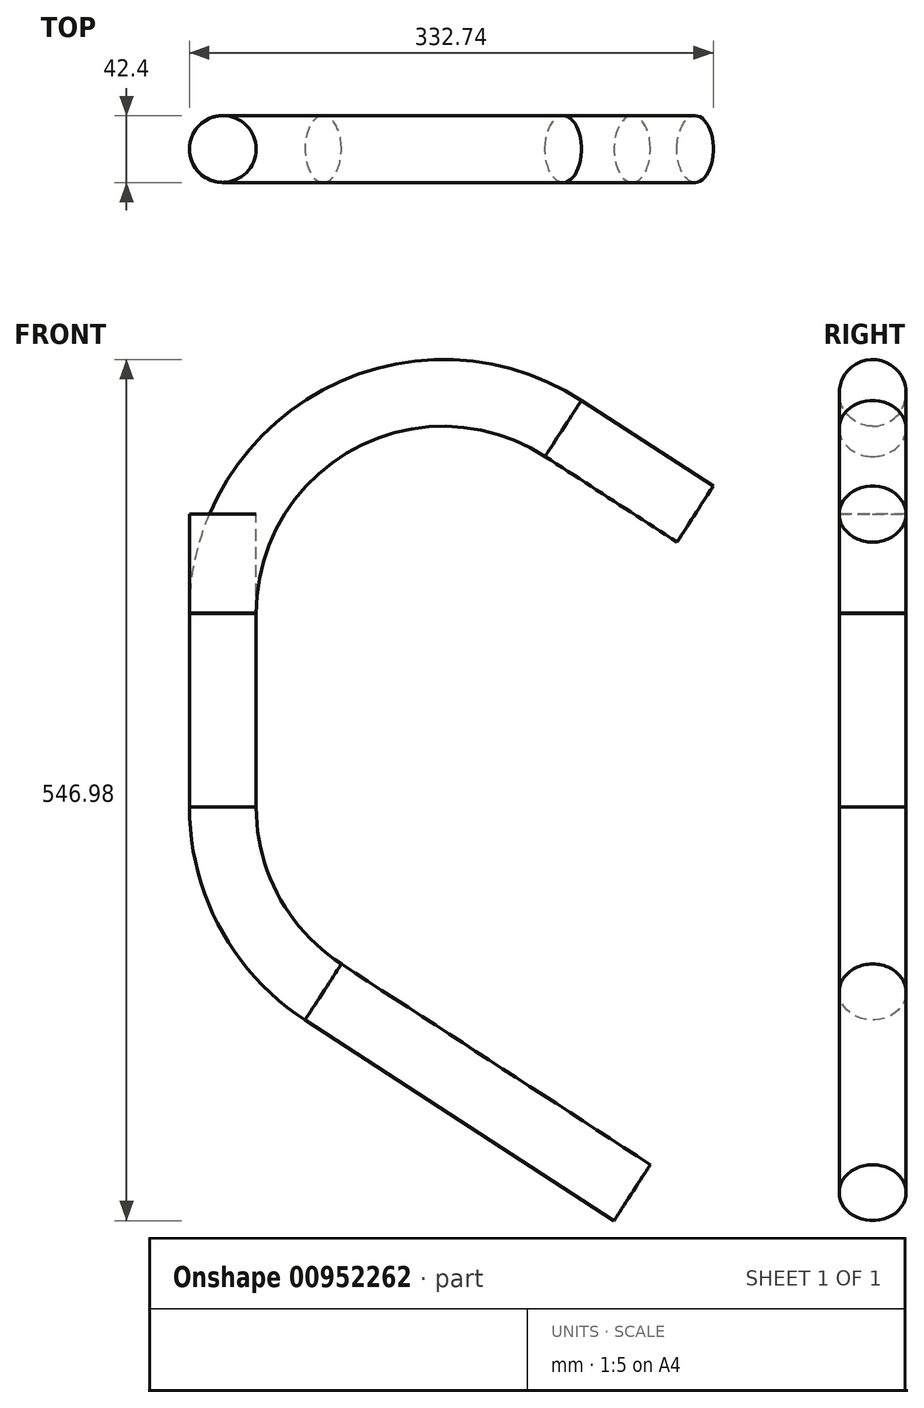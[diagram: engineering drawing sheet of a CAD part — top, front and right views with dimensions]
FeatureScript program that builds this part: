
annotation { "Feature Type Name" : "Feature", "Feature Type Description" : "" }
export const myFeature = defineFeature(function(context is Context, id is Id, definition is map)
    precondition{}
    {
        {
            var Q0;
            Q0=qCreatedBy(makeId("Front.planeOp"),FACE);
            var sketch = newSketch(context, id + "F0", { "sketchPlane" : qUnion([Q0])});
            skLineSegment(sketch, "E0", {"start": v(0, 0) * mm, "end": v(-83.75, 54.39) * mm});
            skLineSegment(sketch, "E1", {"start": v(-300, -63.03) * mm, "end": v(-300, -186.16) * mm});
            skLineSegment(sketch, "E2", {"start": v(-236.25, -303.58) * mm, "end": v(-40, -431.02) * mm});
            skPoint(sketch, "E3.visualSharp", {"position": v(-300, 194.82) * mm});
            skArc(sketch, "E3.filletArc", {"start": v(-83.75, 54.39) * mm, "mid": v(-226.8, 60) * mm, "end": v(-300, -63.03) * mm});
            skPoint(sketch, "E4.visualSharp", {"position": v(-300, -262.18) * mm});
            skArc(sketch, "E4.filletArc", {"start": v(-300, -186.16) * mm, "mid": v(-283.03, -252.97) * mm, "end": v(-236.25, -303.58) * mm});
            skSolve(sketch);
        }
        {
            var Q0;
            Q0=qCreatedBy(makeId("Top.planeOp"),FACE);
            var sketch = newSketch(context, id + "F1", { "sketchPlane" : qUnion([Q0])});
            skLineSegment(sketch, "E5", {"start": v(0, 0) * mm, "end": v(-300, 0) * mm, "construction": true});
            skCircle(sketch, "E6", {"center": v(-300, 0) * mm, "radius": 21.2 * mm});
            skSolve(sketch);
        }
        {
            var Q0;
            Q0=makeQuery(id+"F1.imprint","IMPRINT",FACE,{"disambiguationData":[TD([[makeQuery(id+"F1.imprint","IMPRINT",EDGE,{"derivedFrom":sQuery(id+"F1.wireOp",EDGE,"E6")}),1.0]])]});
            extrude(context, id + "F2", {"entities" : qUnion([Q0]), "oppositeDirection" : true, "depth" : 63 * mm, "hasOffset" : true, "offsetDistance" : 50 * mm});
        }
        {
            var Q0;
            Q0=makeQuery(id+"F2.opExtrude","CAP_FACE",FACE,{"disambiguationData":[OSD([sQuery(id+"F1.wireOp",EDGE,"E6")])],"isStart":false});
            var Q1;
            Q1=sQuery(id+"F0.wireOp",EDGE,"E0");
            var Q2;
            Q2=sQuery(id+"F0.wireOp",EDGE,"E3.filletArc");
            var Q3;
            Q3=sQuery(id+"F0.wireOp",EDGE,"E1");
            var Q4;
            Q4=sQuery(id+"F0.wireOp",EDGE,"E4.filletArc");
            var Q5;
            Q5=sQuery(id+"F0.wireOp",EDGE,"E2");
            sweep(context, id + "F3", {"profiles" : qUnion([Q0]), "path" : qUnion([Q1, Q2, Q3, Q4, Q5])});
        }
    });
